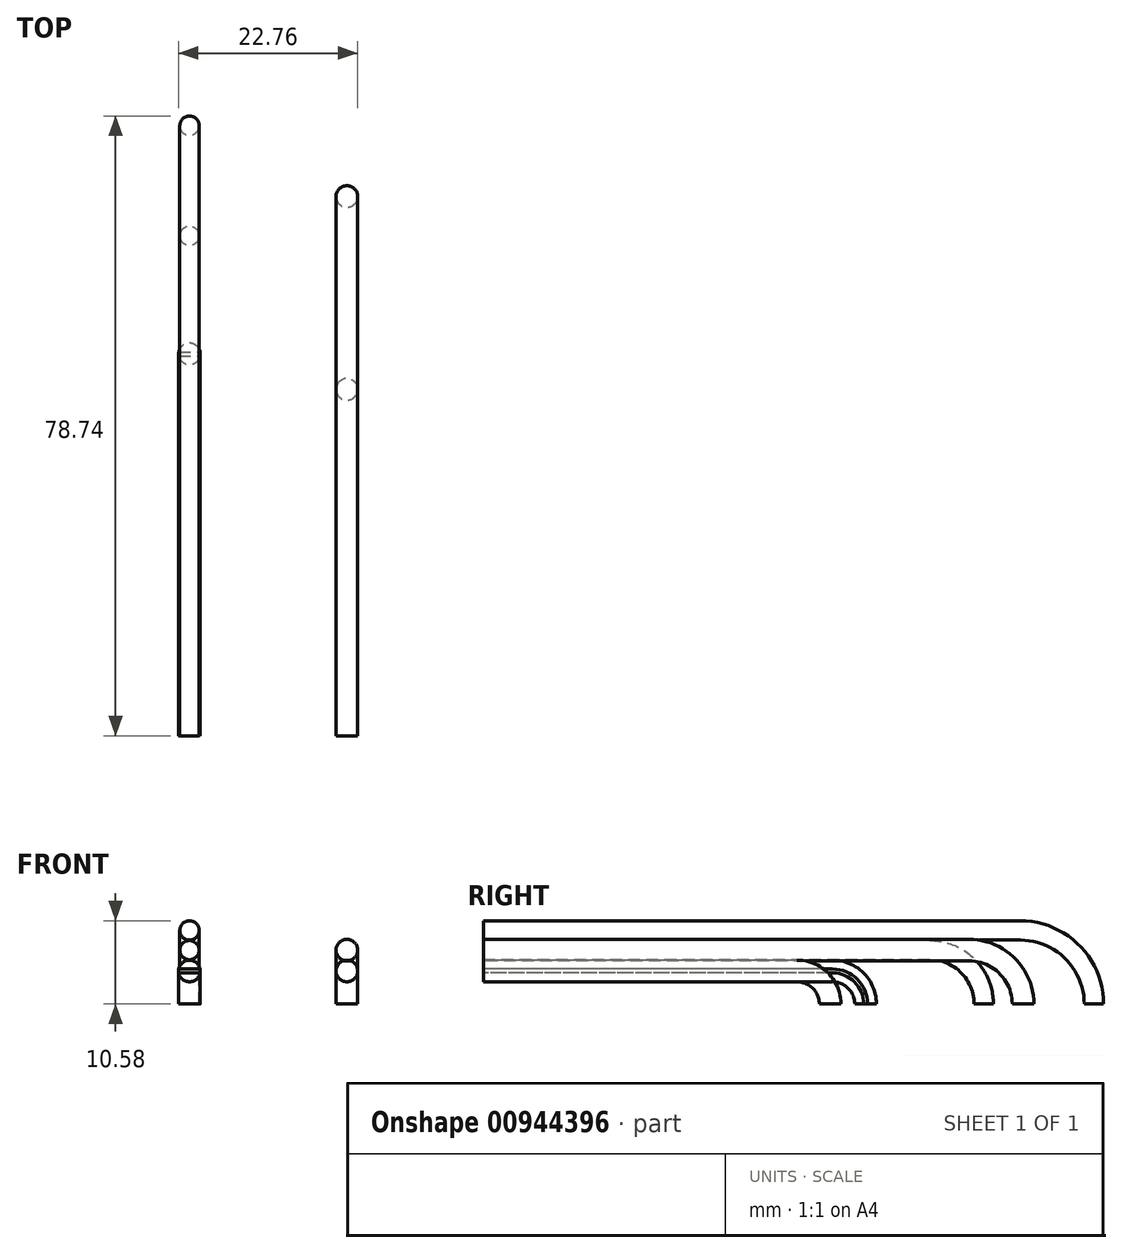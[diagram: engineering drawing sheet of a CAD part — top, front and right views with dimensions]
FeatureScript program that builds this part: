
annotation { "Feature Type Name" : "Feature", "Feature Type Description" : "" }
export const myFeature = defineFeature(function(context is Context, id is Id, definition is map)
    precondition{}
    {
        {
            var Q0;
            Q0=qCreatedBy(makeId("Top.planeOp"),FACE);
            var sketch = newSketch(context, id + "F0", { "sketchPlane" : qUnion([Q0])});
            skLineSegment(sketch, "E0", {"start": v(-10, 76.24) * mm, "end": v(-10, -5.09) * mm, "construction": true});
            skLineSegment(sketch, "E1", {"start": v(10, 71.77) * mm, "end": v(10, -10.19) * mm, "construction": true});
            skCircle(sketch, "E2", {"center": v(-10, 23) * mm, "radius": 1.38 * mm});
            skCircle(sketch, "E3", {"center": v(-10, 29) * mm, "radius": 1.38 * mm});
            skCircle(sketch, "E4", {"center": v(10, 18.5) * mm, "radius": 1.38 * mm});
            skCircle(sketch, "E5", {"center": v(10, 24.5) * mm, "radius": 1.38 * mm});
            skLineSegment(sketch, "E6", {"start": v(-11.35, 23.25) * mm, "end": v(-8.65, 23.25) * mm});
            skLineSegment(sketch, "E7", {"start": v(-11.35, 22.75) * mm, "end": v(-8.65, 22.75) * mm});
            skLineSegment(sketch, "E8", {"start": v(-11.35, 29.25) * mm, "end": v(-8.65, 29.25) * mm});
            skLineSegment(sketch, "E9", {"start": v(-11.35, 28.75) * mm, "end": v(-8.65, 28.75) * mm});
            skCircle(sketch, "E10", {"center": v(-10, 58) * mm, "radius": 1.23 * mm});
            skCircle(sketch, "E11", {"center": v(-10, 44) * mm, "radius": 1.23 * mm});
            skCircle(sketch, "E12", {"center": v(10, 55) * mm, "radius": 1.23 * mm});
            skCircle(sketch, "E13", {"center": v(10, 49) * mm, "radius": 1.38 * mm});
            skSolve(sketch);
        }
        {
            var Q0;
            Q0=qCreatedBy(makeId("Right.planeOp"),FACE);
            cPlane(context, id + "F1", {"entities" : qUnion([Q0]), "cplaneType" : CPlaneType.OFFSET, "offset" : 10 * mm, "oppositeDirection" : true, "width" : 150 * mm, "height" : 150 * mm});
        }
        {
            var Q0;
            Q0=qCreatedBy(makeId("Right.planeOp"),FACE);
            cPlane(context, id + "F2", {"entities" : qUnion([Q0]), "cplaneType" : CPlaneType.OFFSET, "offset" : 10 * mm, "width" : 150 * mm, "height" : 150 * mm});
        }
        {
            var Q0;
            Q0=qCreatedBy(id+"F1.planeOp",FACE);
            var sketch = newSketch(context, id + "F3", { "sketchPlane" : qUnion([Q0])});
            skArc(sketch, "E14", {"start": v(23, 0) * mm, "mid": v(22.59, 0.99) * mm, "end": v(21.6, 1.4) * mm});
            skLineSegment(sketch, "E15", {"start": v(21.6, 1.4) * mm, "end": v(-19.51, 1.4) * mm});
            skArc(sketch, "E16", {"start": v(29, 0) * mm, "mid": v(27.77, 2.97) * mm, "end": v(24.8, 4.2) * mm});
            skLineSegment(sketch, "E17", {"start": v(24.8, 4.2) * mm, "end": v(-19.51, 4.2) * mm});
            skLineSegment(sketch, "E18", {"start": v(37.15, 6.85) * mm, "end": v(-19.51, 6.85) * mm});
            skLineSegment(sketch, "E19", {"start": v(48.65, 9.35) * mm, "end": v(-19.51, 9.35) * mm});
            skArc(sketch, "E20", {"start": v(44, 0) * mm, "mid": v(42, 4.84) * mm, "end": v(37.15, 6.85) * mm});
            skArc(sketch, "E21", {"start": v(58, 0) * mm, "mid": v(55.26, 6.61) * mm, "end": v(48.65, 9.35) * mm});
            skSolve(sketch);
        }
        {
            var Q0;
            Q0=qCreatedBy(id+"F2.planeOp",FACE);
            var sketch = newSketch(context, id + "F4", { "sketchPlane" : qUnion([Q0])});
            skArc(sketch, "E22", {"start": v(18.5, 0) * mm, "mid": v(18.09, 0.99) * mm, "end": v(17.1, 1.4) * mm});
            skArc(sketch, "E23", {"start": v(24.5, 0) * mm, "mid": v(23.27, 2.97) * mm, "end": v(20.3, 4.2) * mm});
            skLineSegment(sketch, "E24", {"start": v(17.1, 1.4) * mm, "end": v(-19.51, 1.4) * mm});
            skLineSegment(sketch, "E25", {"start": v(20.3, 4.2) * mm, "end": v(-19.51, 4.2) * mm});
            skLineSegment(sketch, "E26", {"start": v(42.15, 6.85) * mm, "end": v(-19.51, 6.85) * mm});
            skLineSegment(sketch, "E27", {"start": v(45.65, 9.35) * mm, "end": v(-19.51, 9.35) * mm});
            skArc(sketch, "E28", {"start": v(49, 0) * mm, "mid": v(47, 4.84) * mm, "end": v(42.15, 6.85) * mm});
            skArc(sketch, "E29", {"start": v(55, 0) * mm, "mid": v(52.26, 6.61) * mm, "end": v(45.65, 9.35) * mm});
            skSolve(sketch);
        }
        {
            var Q0;
            Q0=makeQuery(id+"F0.imprint","IMPRINT",FACE,{"disambiguationData":[TD([[makeQuery(id+"F0.imprint","IMPRINT",EDGE,{"derivedFrom":sQuery(id+"F0.wireOp",EDGE,"E11")}),1.0]])]});
            var Q1;
            Q1=sQuery(id+"F3.wireOp",EDGE,"E18");
            var Q2;
            Q2=sQuery(id+"F3.wireOp",EDGE,"E20");
            sweep(context, id + "F5", {"profiles" : qUnion([Q0]), "path" : qUnion([Q1, Q2])});
        }
        {
            var Q0;
            Q0=makeQuery(id+"F0.imprint","IMPRINT",FACE,{"disambiguationData":[TD([[makeQuery(id+"F0.imprint","IMPRINT",EDGE,{"derivedFrom":sQuery(id+"F0.wireOp",EDGE,"E10")}),1.0]])]});
            var Q1;
            Q1=sQuery(id+"F0.wireOp",EDGE,"ZZW9ILuc-Qh0Z-cEP5-6Sod-cu6Z1KOUDuxO");
            var Q2;
            Q2=sQuery(id+"F3.wireOp",EDGE,"E19");
            var Q3;
            Q3=sQuery(id+"F3.wireOp",EDGE,"E21");
            sweep(context, id + "F6", {"profiles" : qUnion([Q0]), "surfaceProfiles" : qUnion([Q1]), "path" : qUnion([Q2, Q3])});
        }
        {
            var Q0;
            Q0=makeQuery(id+"F0.imprint","IMPRINT",FACE,{"disambiguationData":[TD([[makeQuery(id+"F0.imprint","IMPRINT",EDGE,{"derivedFrom":sQuery(id+"F0.wireOp",EDGE,"E13")}),1.0]])]});
            var Q1;
            Q1=sQuery(id+"F4.wireOp",EDGE,"E26");
            var Q2;
            Q2=sQuery(id+"F4.wireOp",EDGE,"E28");
            sweep(context, id + "F7", {"profiles" : qUnion([Q0]), "path" : qUnion([Q1, Q2])});
        }
        {
            var Q0;
            {var subQ0=sQuery(id+"F0.wireOp",EDGE,"E8");Q0=makeQuery(id+"F0.imprint","IMPRINT",FACE,{"disambiguationData":[TD([[makeQuery(id+"F0.imprint","IMPRINT",EDGE,{"derivedFrom":subQ0}),-1.0]])]});}
            var Q1;
            Q1=sQuery(id+"F3.wireOp",EDGE,"E16");
            var Q2;
            Q2=sQuery(id+"F3.wireOp",EDGE,"E17");
            sweep(context, id + "F8", {"profiles" : qUnion([Q0]), "path" : qUnion([Q1, Q2])});
        }
        {
            var Q0;
            Q0=makeQuery(id+"F0.imprint","IMPRINT",FACE,{"disambiguationData":[TD([[makeQuery(id+"F0.imprint","IMPRINT",EDGE,{"derivedFrom":sQuery(id+"F0.wireOp",EDGE,"E5")}),1.0]])]});
            var Q1;
            Q1=sQuery(id+"F4.wireOp",EDGE,"E23");
            var Q2;
            Q2=sQuery(id+"F4.wireOp",EDGE,"E25");
            sweep(context, id + "F9", {"profiles" : qUnion([Q0]), "path" : qUnion([Q1, Q2])});
        }
        {
            var Q0;
            {var subQ0=sQuery(id+"F0.wireOp",EDGE,"E8");Q0=makeQuery(id+"F0.imprint","IMPRINT",FACE,{"disambiguationData":[TD([[makeQuery(id+"F0.imprint","IMPRINT",EDGE,{"derivedFrom":subQ0}),1.0]])]});}
            var Q1;
            Q1=sQuery(id+"F3.wireOp",EDGE,"E16");
            var Q2;
            Q2=sQuery(id+"F3.wireOp",EDGE,"E17");
            sweep(context, id + "F10", {"profiles" : qUnion([Q0]), "path" : qUnion([Q1, Q2])});
        }
        {
            var Q0;
            {var subQ0=sQuery(id+"F0.wireOp",EDGE,"E9");Q0=makeQuery(id+"F0.imprint","IMPRINT",FACE,{"disambiguationData":[TD([[makeQuery(id+"F0.imprint","IMPRINT",EDGE,{"derivedFrom":subQ0}),-1.0]])]});}
            var Q1;
            Q1=sQuery(id+"F3.wireOp",EDGE,"E16");
            var Q2;
            Q2=sQuery(id+"F3.wireOp",EDGE,"E17");
            sweep(context, id + "F11", {"profiles" : qUnion([Q0]), "path" : qUnion([Q1, Q2])});
        }
    });
